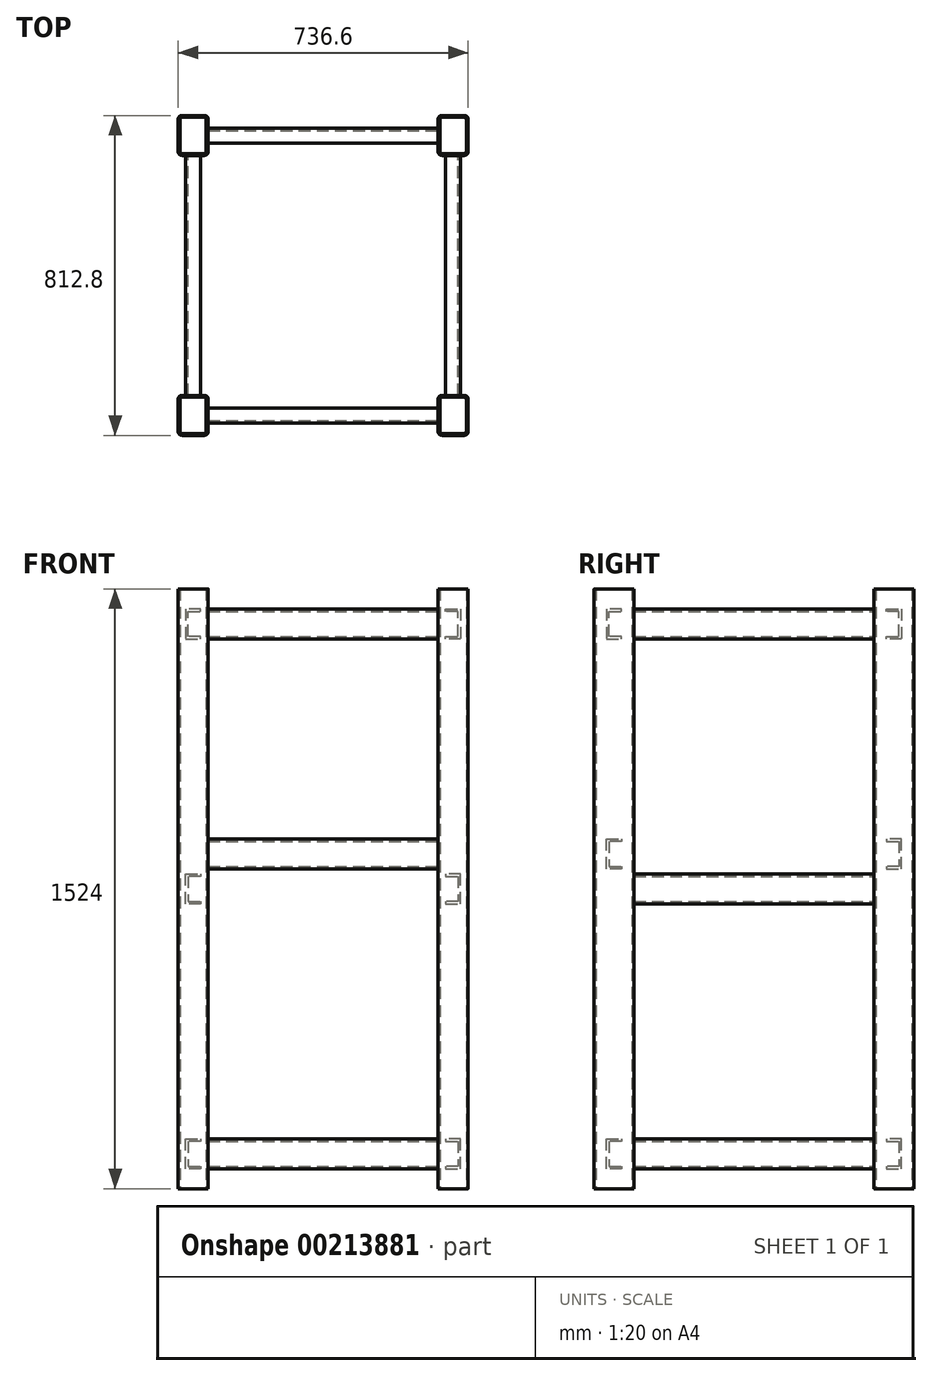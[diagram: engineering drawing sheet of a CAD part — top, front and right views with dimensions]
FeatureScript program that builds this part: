
annotation { "Feature Type Name" : "Feature", "Feature Type Description" : "" }
export const myFeature = defineFeature(function(context is Context, id is Id, definition is map)
    precondition{}
    {
        {
            var Q0;
            Q0=qCreatedBy(makeId("Top.planeOp"),FACE);
            var sketch = newSketch(context, id + "F0", { "sketchPlane" : qUnion([Q0])});
            skLineSegment(sketch, "E0.bottom", {"start": v(301.63, -304.8) * mm, "end": v(358.78, -304.8) * mm});
            skLineSegment(sketch, "E0.top", {"start": v(301.63, -406.4) * mm, "end": v(358.78, -406.4) * mm});
            skLineSegment(sketch, "E0.left", {"start": v(292.1, -314.33) * mm, "end": v(292.1, -396.88) * mm});
            skLineSegment(sketch, "E0.right", {"start": v(368.3, -314.33) * mm, "end": v(368.3, -396.88) * mm});
            skLineSegment(sketch, "E1", {"start": v(292.1, -355.6) * mm, "end": v(368.3, -355.6) * mm, "construction": true});
            skLineSegment(sketch, "E2", {"start": v(330.2, -304.8) * mm, "end": v(330.2, -406.4) * mm, "construction": true});
            skPoint(sketch, "E3.visualSharp", {"position": v(292.1, -304.8) * mm});
            skArc(sketch, "E3.filletArc", {"start": v(301.63, -304.8) * mm, "mid": v(294.89, -307.59) * mm, "end": v(292.1, -314.33) * mm});
            skPoint(sketch, "E4.visualSharp", {"position": v(368.3, -304.8) * mm});
            skArc(sketch, "E4.filletArc", {"start": v(368.3, -314.33) * mm, "mid": v(365.51, -307.59) * mm, "end": v(358.78, -304.8) * mm});
            skPoint(sketch, "E5.visualSharp", {"position": v(368.3, -406.4) * mm});
            skArc(sketch, "E5.filletArc", {"start": v(358.78, -406.4) * mm, "mid": v(365.51, -403.61) * mm, "end": v(368.3, -396.88) * mm});
            skPoint(sketch, "E6.visualSharp", {"position": v(292.1, -406.4) * mm});
            skArc(sketch, "E6.filletArc", {"start": v(292.1, -396.88) * mm, "mid": v(294.89, -403.61) * mm, "end": v(301.63, -406.4) * mm});
            skLineSegment(sketch, "E7.0", {"start": v(301.63, -309.56) * mm, "end": v(358.78, -309.56) * mm});
            skLineSegment(sketch, "E8.0", {"start": v(296.86, -314.33) * mm, "end": v(296.86, -396.88) * mm});
            skLineSegment(sketch, "E9.MirrorCS", {"start": v(363.54, -314.33) * mm, "end": v(363.54, -396.88) * mm});
            skLineSegment(sketch, "E10.MirrorCS", {"start": v(301.63, -401.64) * mm, "end": v(358.78, -401.64) * mm});
            skPoint(sketch, "E11.newPointA", {"position": v(296.86, -314.33) * mm});
            skPoint(sketch, "E11.newPointB", {"position": v(301.63, -309.56) * mm});
            skArc(sketch, "E11.filletArc", {"start": v(301.63, -309.56) * mm, "mid": v(298.26, -310.96) * mm, "end": v(296.86, -314.33) * mm});
            skArc(sketch, "E12.MirrorCS", {"start": v(358.78, -309.56) * mm, "mid": v(362.14, -310.96) * mm, "end": v(363.54, -314.33) * mm});
            skArc(sketch, "E13.MirrorCS", {"start": v(301.63, -401.64) * mm, "mid": v(298.26, -400.24) * mm, "end": v(296.86, -396.88) * mm});
            skArc(sketch, "E14.MirrorCS", {"start": v(358.78, -401.64) * mm, "mid": v(362.14, -400.24) * mm, "end": v(363.54, -396.88) * mm});
            skSolve(sketch);
        }
        {
            var Q0;
            Q0=makeQuery(id+"F0.imprint","IMPRINT",FACE,{"disambiguationData":[TD([[makeQuery(id+"F0.imprint","IMPRINT",EDGE,{"derivedFrom":sQuery(id+"F0.wireOp",EDGE,"E0.bottom")}),-1.0]])]});
            extrude(context, id + "F1", {"entities" : qUnion([Q0]), "depth" : 1524 * mm});
        }
        {
            var Q0;
            Q0=makeQuery(id+"F1.opExtrude","SWEPT_BODY",BODY,{"disambiguationData":[OSD([sQuery(id+"F0.wireOp",EDGE,"E0.bottom"),sQuery(id+"F0.wireOp",EDGE,"E0.top"),sQuery(id+"F0.wireOp",EDGE,"E0.left"),sQuery(id+"F0.wireOp",EDGE,"E0.right"),sQuery(id+"F0.wireOp",EDGE,"E3.filletArc"),sQuery(id+"F0.wireOp",EDGE,"E4.filletArc"),sQuery(id+"F0.wireOp",EDGE,"E5.filletArc"),sQuery(id+"F0.wireOp",EDGE,"E6.filletArc"),sQuery(id+"F0.wireOp",EDGE,"E7.0"),sQuery(id+"F0.wireOp",EDGE,"E8.0"),sQuery(id+"F0.wireOp",EDGE,"E9.MirrorCS"),sQuery(id+"F0.wireOp",EDGE,"E10.MirrorCS"),sQuery(id+"F0.wireOp",EDGE,"E11.filletArc"),sQuery(id+"F0.wireOp",EDGE,"E12.MirrorCS"),sQuery(id+"F0.wireOp",EDGE,"E13.MirrorCS"),sQuery(id+"F0.wireOp",EDGE,"E14.MirrorCS")])]});
            var Q1;
            Q1=qCreatedBy(makeId("Front.planeOp"),FACE);
            mirror(context, id + "F2", {"entities" : qUnion([Q0]), "mirrorPlane" : qUnion([Q1])});
        }
        {
            var Q0;
            Q0=makeQuery(id+"F1.opExtrude","SWEPT_BODY",BODY,{"disambiguationData":[OSD([sQuery(id+"F0.wireOp",EDGE,"E0.bottom"),sQuery(id+"F0.wireOp",EDGE,"E0.top"),sQuery(id+"F0.wireOp",EDGE,"E0.left"),sQuery(id+"F0.wireOp",EDGE,"E0.right"),sQuery(id+"F0.wireOp",EDGE,"E3.filletArc"),sQuery(id+"F0.wireOp",EDGE,"E4.filletArc"),sQuery(id+"F0.wireOp",EDGE,"E5.filletArc"),sQuery(id+"F0.wireOp",EDGE,"E6.filletArc"),sQuery(id+"F0.wireOp",EDGE,"E7.0"),sQuery(id+"F0.wireOp",EDGE,"E8.0"),sQuery(id+"F0.wireOp",EDGE,"E9.MirrorCS"),sQuery(id+"F0.wireOp",EDGE,"E10.MirrorCS"),sQuery(id+"F0.wireOp",EDGE,"E11.filletArc"),sQuery(id+"F0.wireOp",EDGE,"E12.MirrorCS"),sQuery(id+"F0.wireOp",EDGE,"E13.MirrorCS"),sQuery(id+"F0.wireOp",EDGE,"E14.MirrorCS")])]});
            var Q1;
            Q1=makeQuery(id+"F2.opPattern","COPY",BODY,{"derivedFrom":makeQuery(id+"F1.opExtrude","SWEPT_BODY",BODY,{"disambiguationData":[OSD([sQuery(id+"F0.wireOp",EDGE,"E0.bottom"),sQuery(id+"F0.wireOp",EDGE,"E0.top"),sQuery(id+"F0.wireOp",EDGE,"E0.left"),sQuery(id+"F0.wireOp",EDGE,"E0.right"),sQuery(id+"F0.wireOp",EDGE,"E3.filletArc"),sQuery(id+"F0.wireOp",EDGE,"E4.filletArc"),sQuery(id+"F0.wireOp",EDGE,"E5.filletArc"),sQuery(id+"F0.wireOp",EDGE,"E6.filletArc"),sQuery(id+"F0.wireOp",EDGE,"E7.0"),sQuery(id+"F0.wireOp",EDGE,"E8.0"),sQuery(id+"F0.wireOp",EDGE,"E9.MirrorCS"),sQuery(id+"F0.wireOp",EDGE,"E10.MirrorCS"),sQuery(id+"F0.wireOp",EDGE,"E11.filletArc"),sQuery(id+"F0.wireOp",EDGE,"E12.MirrorCS"),sQuery(id+"F0.wireOp",EDGE,"E13.MirrorCS"),sQuery(id+"F0.wireOp",EDGE,"E14.MirrorCS")])]}),"instanceName":"1"});
            var Q2;
            Q2=qCreatedBy(makeId("Right.planeOp"),FACE);
            mirror(context, id + "F3", {"entities" : qUnion([Q0, Q1]), "mirrorPlane" : qUnion([Q2])});
        }
        {
            var Q0;
            Q0=makeQuery(id+"F2.opPattern","COPY",FACE,{"derivedFrom":makeQuery(id+"F1.opExtrude","SWEPT_FACE",FACE,{"disambiguationData":[OSD([sQuery(id+"F0.wireOp",EDGE,"E0.bottom")])]}),"instanceName":"1"});
            var sketch = newSketch(context, id + "F4", { "sketchPlane" : qUnion([Q0])});
            skLineSegment(sketch, "E15", {"start": v(311.15, 50.8) * mm, "end": v(349.25, 50.8) * mm});
            skLineSegment(sketch, "E16", {"start": v(349.25, 50.8) * mm, "end": v(349.25, 127) * mm});
            skLineSegment(sketch, "E17", {"start": v(349.25, 127) * mm, "end": v(311.15, 127) * mm});
            skLineSegment(sketch, "E18", {"start": v(311.15, 127) * mm, "end": v(311.15, 120.65) * mm});
            skLineSegment(sketch, "E19", {"start": v(311.15, 120.65) * mm, "end": v(342.9, 120.65) * mm});
            skLineSegment(sketch, "E20", {"start": v(342.9, 120.65) * mm, "end": v(342.9, 57.15) * mm});
            skLineSegment(sketch, "E21", {"start": v(342.9, 57.15) * mm, "end": v(311.15, 57.15) * mm});
            skLineSegment(sketch, "E22", {"start": v(311.15, 57.15) * mm, "end": v(311.15, 50.8) * mm});
            skSolve(sketch);
        }
        {
            var Q0;
            Q0=makeQuery(id+"F4.imprint","IMPRINT",FACE,{"disambiguationData":[TD([[makeQuery(id+"F4.imprint","IMPRINT",EDGE,{"derivedFrom":sQuery(id+"F4.wireOp",EDGE,"E15")}),1.0]])]});
            extrude(context, id + "F5", {"entities" : qUnion([Q0]), "depth" : 609.6 * mm});
        }
        {
            var Q0;
            Q0=qCreatedBy(makeId("Top.planeOp"),FACE);
            cPlane(context, id + "F6", {"entities" : qUnion([Q0]), "cplaneType" : CPlaneType.OFFSET, "offset" : 762 * mm, "width" : 152.4 * mm, "height" : 152.4 * mm});
        }
        {
            var Q0;
            Q0=makeQuery(id+"F5.opExtrude","SWEPT_BODY",BODY,{"disambiguationData":[OSD([sQuery(id+"F4.wireOp",EDGE,"E15"),sQuery(id+"F4.wireOp",EDGE,"E16"),sQuery(id+"F4.wireOp",EDGE,"E17"),sQuery(id+"F4.wireOp",EDGE,"E18"),sQuery(id+"F4.wireOp",EDGE,"E19"),sQuery(id+"F4.wireOp",EDGE,"E20"),sQuery(id+"F4.wireOp",EDGE,"E21"),sQuery(id+"F4.wireOp",EDGE,"E22")])]});
            var Q1;
            Q1=qCreatedBy(id+"F6.planeOp",FACE);
            mirror(context, id + "F7", {"entities" : qUnion([Q0]), "mirrorPlane" : qUnion([Q1])});
        }
        {
            var Q0;
            Q0=makeQuery(id+"F5.opExtrude","SWEPT_BODY",BODY,{"disambiguationData":[OSD([sQuery(id+"F4.wireOp",EDGE,"E15"),sQuery(id+"F4.wireOp",EDGE,"E16"),sQuery(id+"F4.wireOp",EDGE,"E17"),sQuery(id+"F4.wireOp",EDGE,"E18"),sQuery(id+"F4.wireOp",EDGE,"E19"),sQuery(id+"F4.wireOp",EDGE,"E20"),sQuery(id+"F4.wireOp",EDGE,"E21"),sQuery(id+"F4.wireOp",EDGE,"E22")])]});
            var Q1;
            Q1=makeQuery(id+"F1.opExtrude","SWEPT_EDGE",EDGE,{"disambiguationData":[OSD([sQuery(id+"F0.wireOp",EDGE,"E0.right"),sQuery(id+"F0.wireOp",EDGE,"E4.filletArc")])]});
            var Q2;
            Q2=makeQuery(id+"F1.opExtrude","SWEPT_EDGE",EDGE,{"disambiguationData":[OSD([sQuery(id+"F0.wireOp",EDGE,"E0.right"),sQuery(id+"F0.wireOp",EDGE,"E4.filletArc")])]});
            transform(context, id + "F8", {"entities" : qUnion([Q0]), "transformType" : TransformType.TRANSLATION_DISTANCE, "transformDirection" : qUnion([Q2]), "distance" : 673.1 * mm, "oppositeDirection" : true, "makeCopy" : true});
        }
        {
            var Q0;
            Q0=makeQuery(id+"F8.opPattern","COPY",BODY,{"derivedFrom":makeQuery(id+"F5.opExtrude","SWEPT_BODY",BODY,{"disambiguationData":[OSD([sQuery(id+"F4.wireOp",EDGE,"E15"),sQuery(id+"F4.wireOp",EDGE,"E16"),sQuery(id+"F4.wireOp",EDGE,"E17"),sQuery(id+"F4.wireOp",EDGE,"E18"),sQuery(id+"F4.wireOp",EDGE,"E19"),sQuery(id+"F4.wireOp",EDGE,"E20"),sQuery(id+"F4.wireOp",EDGE,"E21"),sQuery(id+"F4.wireOp",EDGE,"E22")])]}),"instanceName":"1"});
            var Q1;
            Q1=makeQuery(id+"F7.opPattern","COPY",BODY,{"derivedFrom":makeQuery(id+"F5.opExtrude","SWEPT_BODY",BODY,{"disambiguationData":[OSD([sQuery(id+"F4.wireOp",EDGE,"E15"),sQuery(id+"F4.wireOp",EDGE,"E16"),sQuery(id+"F4.wireOp",EDGE,"E17"),sQuery(id+"F4.wireOp",EDGE,"E18"),sQuery(id+"F4.wireOp",EDGE,"E19"),sQuery(id+"F4.wireOp",EDGE,"E20"),sQuery(id+"F4.wireOp",EDGE,"E21"),sQuery(id+"F4.wireOp",EDGE,"E22")])]}),"instanceName":"1"});
            var Q2;
            Q2=makeQuery(id+"F5.opExtrude","SWEPT_BODY",BODY,{"disambiguationData":[OSD([sQuery(id+"F4.wireOp",EDGE,"E15"),sQuery(id+"F4.wireOp",EDGE,"E16"),sQuery(id+"F4.wireOp",EDGE,"E17"),sQuery(id+"F4.wireOp",EDGE,"E18"),sQuery(id+"F4.wireOp",EDGE,"E19"),sQuery(id+"F4.wireOp",EDGE,"E20"),sQuery(id+"F4.wireOp",EDGE,"E21"),sQuery(id+"F4.wireOp",EDGE,"E22")])]});
            var Q3;
            Q3=qCreatedBy(makeId("Right.planeOp"),FACE);
            mirror(context, id + "F9", {"entities" : qUnion([Q0, Q1, Q2]), "mirrorPlane" : qUnion([Q3])});
        }
        {
            var Q0;
            Q0=makeQuery(id+"F1.opExtrude","SWEPT_FACE",FACE,{"disambiguationData":[OSD([sQuery(id+"F0.wireOp",EDGE,"E0.left")])]});
            var sketch = newSketch(context, id + "F10", { "sketchPlane" : qUnion([Q0])});
            skLineSegment(sketch, "E23", {"start": v(336.55, 50.8) * mm, "end": v(374.65, 50.8) * mm});
            skLineSegment(sketch, "E24", {"start": v(374.65, 50.8) * mm, "end": v(374.65, 127) * mm});
            skLineSegment(sketch, "E25", {"start": v(374.65, 127) * mm, "end": v(336.55, 127) * mm});
            skLineSegment(sketch, "E26", {"start": v(336.55, 127) * mm, "end": v(336.55, 120.65) * mm});
            skLineSegment(sketch, "E27", {"start": v(336.55, 120.65) * mm, "end": v(368.3, 120.65) * mm});
            skLineSegment(sketch, "E28", {"start": v(368.3, 120.65) * mm, "end": v(368.3, 57.15) * mm});
            skLineSegment(sketch, "E29", {"start": v(368.3, 57.15) * mm, "end": v(336.55, 57.15) * mm});
            skLineSegment(sketch, "E30", {"start": v(336.55, 57.15) * mm, "end": v(336.55, 50.8) * mm});
            skSolve(sketch);
        }
        {
            var Q0;
            Q0=makeQuery(id+"F10.imprint","IMPRINT",FACE,{"disambiguationData":[TD([[makeQuery(id+"F10.imprint","IMPRINT",EDGE,{"derivedFrom":sQuery(id+"F10.wireOp",EDGE,"E23")}),1.0]])]});
            extrude(context, id + "F11", {"entities" : qUnion([Q0]), "depth" : 584.2 * mm});
        }
        {
            var Q0;
            Q0=makeQuery(id+"F11.opExtrude","SWEPT_BODY",BODY,{"disambiguationData":[OSD([sQuery(id+"F10.wireOp",EDGE,"E23"),sQuery(id+"F10.wireOp",EDGE,"E24"),sQuery(id+"F10.wireOp",EDGE,"E25"),sQuery(id+"F10.wireOp",EDGE,"E26"),sQuery(id+"F10.wireOp",EDGE,"E27"),sQuery(id+"F10.wireOp",EDGE,"E28"),sQuery(id+"F10.wireOp",EDGE,"E29"),sQuery(id+"F10.wireOp",EDGE,"E30")])]});
            var Q1;
            Q1=makeQuery(id+"F3.opPattern","COPY",EDGE,{"derivedFrom":makeQuery(id+"F1.opExtrude","SWEPT_EDGE",EDGE,{"disambiguationData":[OSD([sQuery(id+"F0.wireOp",EDGE,"E0.left"),sQuery(id+"F0.wireOp",EDGE,"E3.filletArc")])]}),"instanceName":"1"});
            transform(context, id + "F12", {"entities" : qUnion([Q0]), "transformType" : TransformType.TRANSLATION_DISTANCE, "transformDirection" : qUnion([Q1]), "distance" : 762 * mm, "oppositeDirection" : true, "makeCopy" : true});
        }
        {
            var Q0;
            Q0=makeQuery(id+"F11.opExtrude","SWEPT_BODY",BODY,{"disambiguationData":[OSD([sQuery(id+"F10.wireOp",EDGE,"E23"),sQuery(id+"F10.wireOp",EDGE,"E24"),sQuery(id+"F10.wireOp",EDGE,"E25"),sQuery(id+"F10.wireOp",EDGE,"E26"),sQuery(id+"F10.wireOp",EDGE,"E27"),sQuery(id+"F10.wireOp",EDGE,"E28"),sQuery(id+"F10.wireOp",EDGE,"E29"),sQuery(id+"F10.wireOp",EDGE,"E30")])]});
            var Q1;
            Q1=qCreatedBy(id+"F6.planeOp",FACE);
            mirror(context, id + "F13", {"entities" : qUnion([Q0]), "mirrorPlane" : qUnion([Q1])});
        }
        {
            var Q0;
            Q0=makeQuery(id+"F11.opExtrude","SWEPT_BODY",BODY,{"disambiguationData":[OSD([sQuery(id+"F10.wireOp",EDGE,"E23"),sQuery(id+"F10.wireOp",EDGE,"E24"),sQuery(id+"F10.wireOp",EDGE,"E25"),sQuery(id+"F10.wireOp",EDGE,"E26"),sQuery(id+"F10.wireOp",EDGE,"E27"),sQuery(id+"F10.wireOp",EDGE,"E28"),sQuery(id+"F10.wireOp",EDGE,"E29"),sQuery(id+"F10.wireOp",EDGE,"E30")])]});
            var Q1;
            Q1=makeQuery(id+"F12.opPattern","COPY",BODY,{"derivedFrom":makeQuery(id+"F11.opExtrude","SWEPT_BODY",BODY,{"disambiguationData":[OSD([sQuery(id+"F10.wireOp",EDGE,"E23"),sQuery(id+"F10.wireOp",EDGE,"E24"),sQuery(id+"F10.wireOp",EDGE,"E25"),sQuery(id+"F10.wireOp",EDGE,"E26"),sQuery(id+"F10.wireOp",EDGE,"E27"),sQuery(id+"F10.wireOp",EDGE,"E28"),sQuery(id+"F10.wireOp",EDGE,"E29"),sQuery(id+"F10.wireOp",EDGE,"E30")])]}),"instanceName":"1"});
            var Q2;
            Q2=makeQuery(id+"F13.opPattern","COPY",BODY,{"derivedFrom":makeQuery(id+"F11.opExtrude","SWEPT_BODY",BODY,{"disambiguationData":[OSD([sQuery(id+"F10.wireOp",EDGE,"E23"),sQuery(id+"F10.wireOp",EDGE,"E24"),sQuery(id+"F10.wireOp",EDGE,"E25"),sQuery(id+"F10.wireOp",EDGE,"E26"),sQuery(id+"F10.wireOp",EDGE,"E27"),sQuery(id+"F10.wireOp",EDGE,"E28"),sQuery(id+"F10.wireOp",EDGE,"E29"),sQuery(id+"F10.wireOp",EDGE,"E30")])]}),"instanceName":"1"});
            var Q3;
            Q3=qCreatedBy(makeId("Front.planeOp"),FACE);
            mirror(context, id + "F14", {"entities" : qUnion([Q0, Q1, Q2]), "mirrorPlane" : qUnion([Q3])});
        }
        {
            var Q0;
            Q0=makeQuery(id+"F11.opExtrude","SWEPT_FACE",FACE,{"disambiguationData":[OSD([sQuery(id+"F10.wireOp",EDGE,"E24")])]});
            cPlane(context, id + "F15", {"entities" : qUnion([Q0]), "cplaneType" : CPlaneType.OFFSET, "offset" : 127 * mm, "width" : 152.4 * mm, "height" : 152.4 * mm});
        }
        {
            var Q0;
            Q0=qCreatedBy(id+"F15.planeOp",FACE);
            var sketch = newSketch(context, id + "F16", { "sketchPlane" : qUnion([Q0])});
            skCircle(sketch, "E31", {"center": v(0, 351.01) * mm, "radius": 71.41 * mm});
            skSolve(sketch);
        }
        {
            var Q0;
            Q0=makeQuery(id+"F16.imprint","IMPRINT",FACE,{"disambiguationData":[TD([[makeQuery(id+"F16.imprint","IMPRINT",EDGE,{"derivedFrom":sQuery(id+"F16.wireOp",EDGE,"E31")}),1.0]])]});
            extrude(context, id + "F17", {"entities" : qUnion([Q0]), "depth" : 320.04 * mm});
        }
        {
            var Q0;
            Q0=makeQuery(id+"F17.opExtrude","SWEPT_BODY",BODY,{"disambiguationData":[OSD([sQuery(id+"F16.wireOp",EDGE,"E31")])]});
            deleteBodies(context, id + "F18", {"entities" : qUnion([Q0])});
        }
    });
